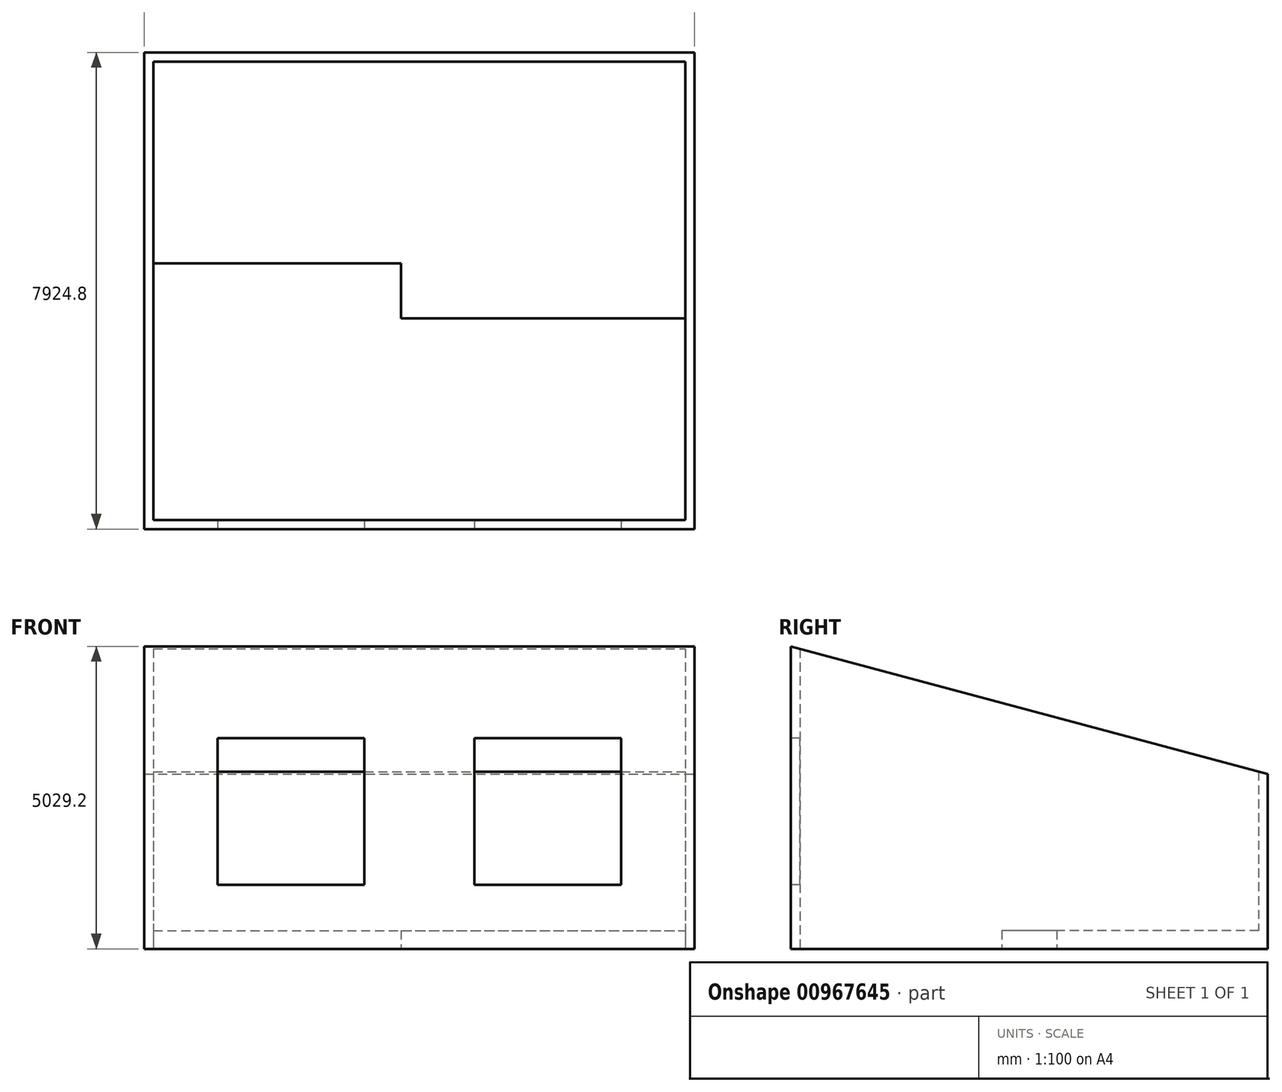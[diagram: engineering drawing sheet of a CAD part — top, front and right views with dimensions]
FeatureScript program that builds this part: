
annotation { "Feature Type Name" : "Feature", "Feature Type Description" : "" }
export const myFeature = defineFeature(function(context is Context, id is Id, definition is map)
    precondition{}
    {
        {
            var Q0;
            Q0=qCreatedBy(makeId("Top.planeOp"),FACE);
            var sketch = newSketch(context, id + "F0", { "sketchPlane" : qUnion([Q0])});
            skLineSegment(sketch, "E0.bottom", {"start": v(-4572, 3962.4) * mm, "end": v(4572, 3962.4) * mm});
            skLineSegment(sketch, "E0.top", {"start": v(-4572, -3962.4) * mm, "end": v(4572, -3962.4) * mm});
            skLineSegment(sketch, "E0.left", {"start": v(-4572, 3962.4) * mm, "end": v(-4572, -3962.4) * mm});
            skLineSegment(sketch, "E0.right", {"start": v(4572, 3962.4) * mm, "end": v(4572, -3962.4) * mm});
            skPoint(sketch, "E0.middle", {"position": v(0, 0) * mm});
            skSolve(sketch);
        }
        {
            var Q0;
            Q0=makeQuery(id+"F0.imprint","IMPRINT",FACE,{"disambiguationData":[TD([[makeQuery(id+"F0.imprint","IMPRINT",EDGE,{"derivedFrom":sQuery(id+"F0.wireOp",EDGE,"E0.bottom")}),-1.0]])]});
            extrude(context, id + "F1", {"entities" : qUnion([Q0]), "depth" : 7620 * mm, "offsetDistance" : 30.48 * mm});
        }
        {
            var Q0;
            Q0=makeQuery(id+"F1.opExtrude","SWEPT_FACE",FACE,{"disambiguationData":[OSD([sQuery(id+"F0.wireOp",EDGE,"E0.right")])]});
            var sketch = newSketch(context, id + "F2", { "sketchPlane" : qUnion([Q0])});
            skLineSegment(sketch, "E1", {"start": v(-3962.4, 7620) * mm, "end": v(3962.4, 5496.56) * mm});
            skLineSegment(sketch, "E2", {"start": v(3962.4, 5496.56) * mm, "end": v(3962.4, 7620) * mm});
            skLineSegment(sketch, "E3", {"start": v(3962.4, 7620) * mm, "end": v(-3962.4, 7620) * mm});
            skSolve(sketch);
        }
        {
            var Q0;
            Q0=qSketchRegion(id+"F2",true);
            extrude(context, id + "F3", {"entities" : qUnion([Q0]), "operationType" : NewBodyOperationType.REMOVE, "endBound" : BoundingType.THROUGH_ALL, "oppositeDirection" : true, "depth" : 30.48 * mm, "offsetDistance" : 30.48 * mm});
        }
        {
            var Q0;
            Q0=makeQuery(id+"F3.boolean.opBoolean","COPY",FACE,{"derivedFrom":makeQuery(id+"F3.opExtrude","SWEPT_FACE",FACE,{"disambiguationData":[OSD([sQuery(id+"F2.wireOp",EDGE,"E1")])]})});
            shell(context, id + "F4", {"entities" : qUnion([Q0]), "thickness" : 152.4 * mm});
        }
        {
            var Q0;
            Q0=makeQuery(id+"F1.opExtrude","SWEPT_FACE",FACE,{"disambiguationData":[OSD([sQuery(id+"F0.wireOp",EDGE,"E0.top")])]});
            var sketch = newSketch(context, id + "F5", { "sketchPlane" : qUnion([Q0])});
            skLineSegment(sketch, "E4.bottom", {"start": v(457.2, 2286) * mm, "end": v(-457.2, 2286) * mm});
            skLineSegment(sketch, "E4.top", {"start": v(457.2, 152.4) * mm, "end": v(-457.2, 152.4) * mm});
            skLineSegment(sketch, "E4.left", {"start": v(457.2, 2286) * mm, "end": v(457.2, 152.4) * mm});
            skLineSegment(sketch, "E4.right", {"start": v(-457.2, 2286) * mm, "end": v(-457.2, 152.4) * mm});
            skPoint(sketch, "E4.middle", {"position": v(0, 1219.2) * mm});
            skLineSegment(sketch, "E5.bottom", {"start": v(-3352.8, 3657.6) * mm, "end": v(-914.4, 3657.6) * mm});
            skLineSegment(sketch, "E5.top", {"start": v(-3352.8, 6096) * mm, "end": v(-914.4, 6096) * mm});
            skLineSegment(sketch, "E5.left", {"start": v(-3352.8, 3657.6) * mm, "end": v(-3352.8, 6096) * mm});
            skLineSegment(sketch, "E5.right", {"start": v(-914.4, 3657.6) * mm, "end": v(-914.4, 6096) * mm});
            skPoint(sketch, "E5.middle", {"position": v(-2133.6, 4876.8) * mm});
            skLineSegment(sketch, "E6.bottom", {"start": v(914.4, 3657.6) * mm, "end": v(3352.8, 3657.6) * mm});
            skLineSegment(sketch, "E6.top", {"start": v(914.4, 6096) * mm, "end": v(3352.8, 6096) * mm});
            skLineSegment(sketch, "E6.left", {"start": v(914.4, 3657.6) * mm, "end": v(914.4, 6096) * mm});
            skLineSegment(sketch, "E6.right", {"start": v(3352.8, 3657.6) * mm, "end": v(3352.8, 6096) * mm});
            skPoint(sketch, "E6.middle", {"position": v(2133.6, 4876.8) * mm});
            skLineSegment(sketch, "E7.bottom", {"start": v(-3352.8, 2438.4) * mm, "end": v(-1524, 2438.4) * mm});
            skLineSegment(sketch, "E7.top", {"start": v(-3352.8, 914.4) * mm, "end": v(-1524, 914.4) * mm});
            skLineSegment(sketch, "E7.left", {"start": v(-3352.8, 2438.4) * mm, "end": v(-3352.8, 914.4) * mm});
            skLineSegment(sketch, "E7.right", {"start": v(-1524, 2438.4) * mm, "end": v(-1524, 914.4) * mm});
            skPoint(sketch, "E7.middle", {"position": v(-2438.4, 1676.4) * mm});
            skLineSegment(sketch, "E8.bottom", {"start": v(1524, 2438.4) * mm, "end": v(3352.8, 2438.4) * mm});
            skLineSegment(sketch, "E8.top", {"start": v(1524, 914.4) * mm, "end": v(3352.8, 914.4) * mm});
            skLineSegment(sketch, "E8.left", {"start": v(1524, 2438.4) * mm, "end": v(1524, 914.4) * mm});
            skLineSegment(sketch, "E8.right", {"start": v(3352.8, 2438.4) * mm, "end": v(3352.8, 914.4) * mm});
            skPoint(sketch, "E8.middle", {"position": v(2438.4, 1676.4) * mm});
            skLineSegment(sketch, "E9", {"start": v(-3352.8, 914.4) * mm, "end": v(-4572, 914.4) * mm, "construction": true});
            skLineSegment(sketch, "E10", {"start": v(3352.8, 914.4) * mm, "end": v(4572, 914.4) * mm, "construction": true});
            skSolve(sketch);
        }
        {
            var Q0;
            Q0=qSketchRegion(id+"F5",true);
            extrude(context, id + "F6", {"entities" : qUnion([Q0]), "operationType" : NewBodyOperationType.REMOVE, "endBound" : BoundingType.UP_TO_NEXT, "oppositeDirection" : true, "depth" : 30.48 * mm, "offsetDistance" : 30.48 * mm});
        }
        {
            var Q0;
            Q0=makeQuery(id+"F6.boolean.opBoolean","MERGE",FACE,{"derivedFrom":[makeQuery(id+"F4.opShell","OFFSET_FACE",FACE,{"disambiguationData":[OSD([sQuery(id+"F0.wireOp",EDGE,"E0.bottom"),sQuery(id+"F0.wireOp",EDGE,"E0.top"),sQuery(id+"F0.wireOp",EDGE,"E0.left"),sQuery(id+"F0.wireOp",EDGE,"E0.right")])]})],"fromTools":[makeQuery(id+"F6.opExtrude","SWEPT_FACE",FACE,{"disambiguationData":[OSD([sQuery(id+"F5.wireOp",EDGE,"E4.top")])]})]});
            cPlane(context, id + "F7", {"entities" : qUnion([Q0]), "cplaneType" : CPlaneType.OFFSET, "offset" : 2438.4 * mm, "width" : 152.4 * mm, "height" : 152.4 * mm});
        }
        {
            var Q0;
            Q0=qCreatedBy(id+"F7.planeOp",FACE);
            var sketch = newSketch(context, id + "F8", { "sketchPlane" : qUnion([Q0])});
            skLineSegment(sketch, "E11.bottom", {"start": v(-4419.6, 3810) * mm, "end": v(4419.6, 3810) * mm});
            skLineSegment(sketch, "E11.top", {"start": v(-304.8, -457.2) * mm, "end": v(4419.6, -457.2) * mm});
            skLineSegment(sketch, "E11.left", {"start": v(-4419.6, 3810) * mm, "end": v(-4419.6, 457.2) * mm});
            skLineSegment(sketch, "E11.right", {"start": v(4419.6, 3810) * mm, "end": v(4419.6, -457.2) * mm});
            skLineSegment(sketch, "E12", {"start": v(-4419.6, 457.2) * mm, "end": v(-304.8, 457.2) * mm});
            skLineSegment(sketch, "E13", {"start": v(-304.8, 457.2) * mm, "end": v(-304.8, -457.2) * mm});
            skSolve(sketch);
        }
        {
            var Q0;
            Q0=qSketchRegion(id+"F8",true);
            extrude(context, id + "F9", {"entities" : qUnion([Q0]), "operationType" : NewBodyOperationType.ADD, "depth" : 304.8 * mm, "offsetDistance" : 30.48 * mm});
        }
        {
            var Q0;
            Q0=makeQuery(id+"F1.opExtrude","SWEPT_FACE",FACE,{"disambiguationData":[OSD([sQuery(id+"F0.wireOp",EDGE,"E0.left")])]});
            var sketch = newSketch(context, id + "F10", { "sketchPlane" : qUnion([Q0])});
            skLineSegment(sketch, "E14.bottom", {"start": v(-3962.4, 0) * mm, "end": v(3962.4, 0) * mm});
            skLineSegment(sketch, "E14.top", {"start": v(-3962.4, 2590.8) * mm, "end": v(3962.4, 2590.8) * mm});
            skLineSegment(sketch, "E14.left", {"start": v(-3962.4, 0) * mm, "end": v(-3962.4, 2590.8) * mm});
            skLineSegment(sketch, "E14.right", {"start": v(3962.4, 0) * mm, "end": v(3962.4, 2590.8) * mm});
            skSolve(sketch);
        }
        {
            var Q0;
            Q0 = qSketchRegion(id + "F10", true);
            extrude(context, id + "F11", {"entities" : qUnion([Q0]), "operationType" : NewBodyOperationType.REMOVE, "endBound" : BoundingType.THROUGH_ALL, "oppositeDirection" : true, "depth" : 30.48 * mm, "offsetDistance" : 30.48 * mm});
        }
    });
